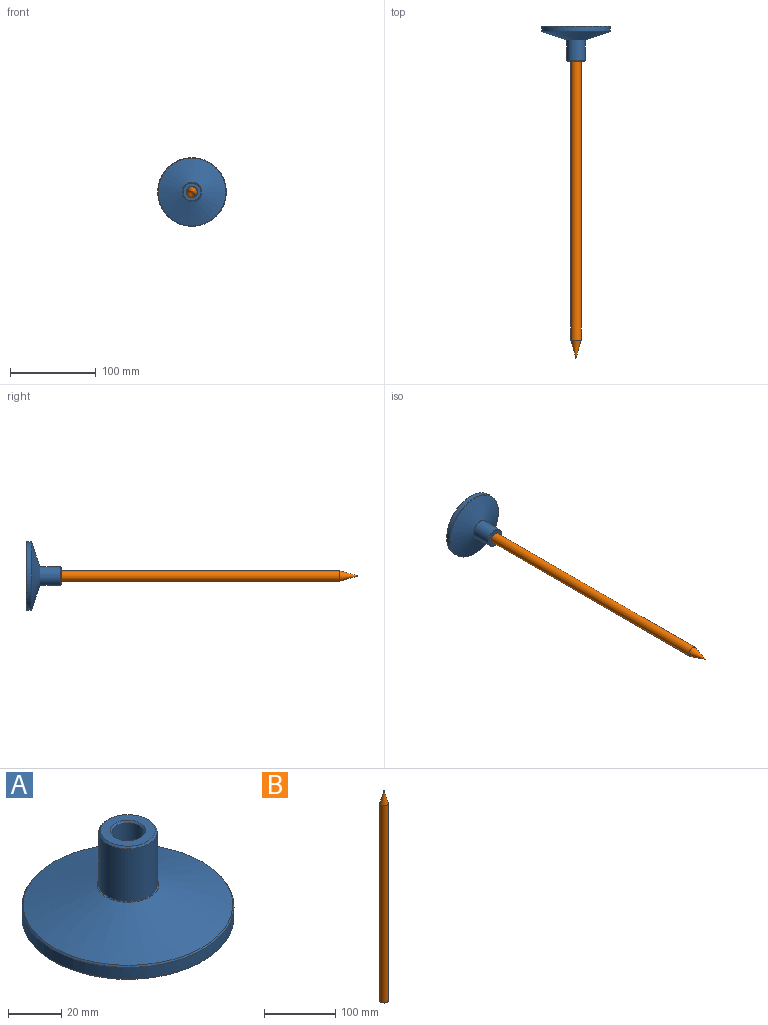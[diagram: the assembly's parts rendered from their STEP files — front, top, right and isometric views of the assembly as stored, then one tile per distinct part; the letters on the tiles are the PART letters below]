
ASSEMBLY  parts=2 mates=1
PART A: 18 faces, bbox 80x80x41 mm
  f0: cylinder r=40mm len=80mm, axis (0,0,-1), area 1333.4mm2, adj f14,f15
  f1: plane 78.61x78.61mm, normal (0,0,-1), area 4352.8mm2, adj f14,f17
  f2: cone r=40mm half-angle=71.5deg, axis (0,0,-1), area 4729.2mm2, adj f3,f15
  f3: plane 23.22x23.22mm, normal (0,0,1), area 43.1mm2, adj f2,f4
  f4: cylinder r=11mm len=24.31mm, axis (0,0,-1), area 1679.9mm2, adj f3,f13
  f5: plane 20.61x20.61mm, normal (0,0,1), area 192.8mm2, adj f12,f13
  f6: cylinder r=6mm len=24.31mm, axis (0,0,1), area 916.3mm2, adj f7,f12
  f7: plane 12x12mm, normal (0,0,1), area 113.1mm2, adj f6
  f8: cylinder r=12.38mm len=24.75mm, axis (0,0,-1), area 291.6mm2, adj f9,f17
  f9: plane 24.75x24.75mm, normal (0,0,-1), area 417.5mm2, adj f8,f16
  f10: cylinder r=4.25mm len=8.5mm, axis (0,0,-1), area 86.8mm2, adj f11,f16
  f11: plane 8.5x8.5mm, normal (0,0,-1), area 56.7mm2, adj f10
  f12: cone r=6mm half-angle=45deg, axis (0,0,1), area 39.2mm2, adj f5,f6
  f13: cone r=10.31mm half-angle=45deg, axis (0,0,-1), area 65.7mm2, adj f4,f5
  f14: cone r=40mm half-angle=45deg, axis (0,0,1), area 244.7mm2, adj f0,f1
  f15: cone r=39.53mm half-angle=35.8deg, axis (0,0,-1), area 202.8mm2, adj f0,f2
  f16: cone r=4.25mm half-angle=45deg, axis (0,0,-1), area 9.7mm2, adj f9,f10
  f17: cone r=12.38mm half-angle=45deg, axis (0,0,-1), area 27.8mm2, adj f1,f8
PART B: 4 faces, bbox 12x12x359.5 mm
  f0: cylinder r=6mm len=338.5mm, axis (0,0,-1), area 12761.1mm2, adj f1,f2
  f1: plane 12x12mm, normal (0,0,-1), area 113.1mm2, adj f0
  f2: cone r=6mm half-angle=15.7deg, axis (0,0,-1), area 416.6mm2, adj f0,f3
  f3: plane 0.15x0.15mm, normal (0,0,1), area 0mm2, adj f2
PLACE A rot(axis=(1,0,0),90deg) t=(0,0,0)mm
PLACE B rot(axis=(0.52,0.61,-0.61),125.4deg) t=(0,-28.38,0)mm
MATE cylindrical B.f0 <-> A.f4  axis (0,1,0) through (0,-28.38,0)mm
